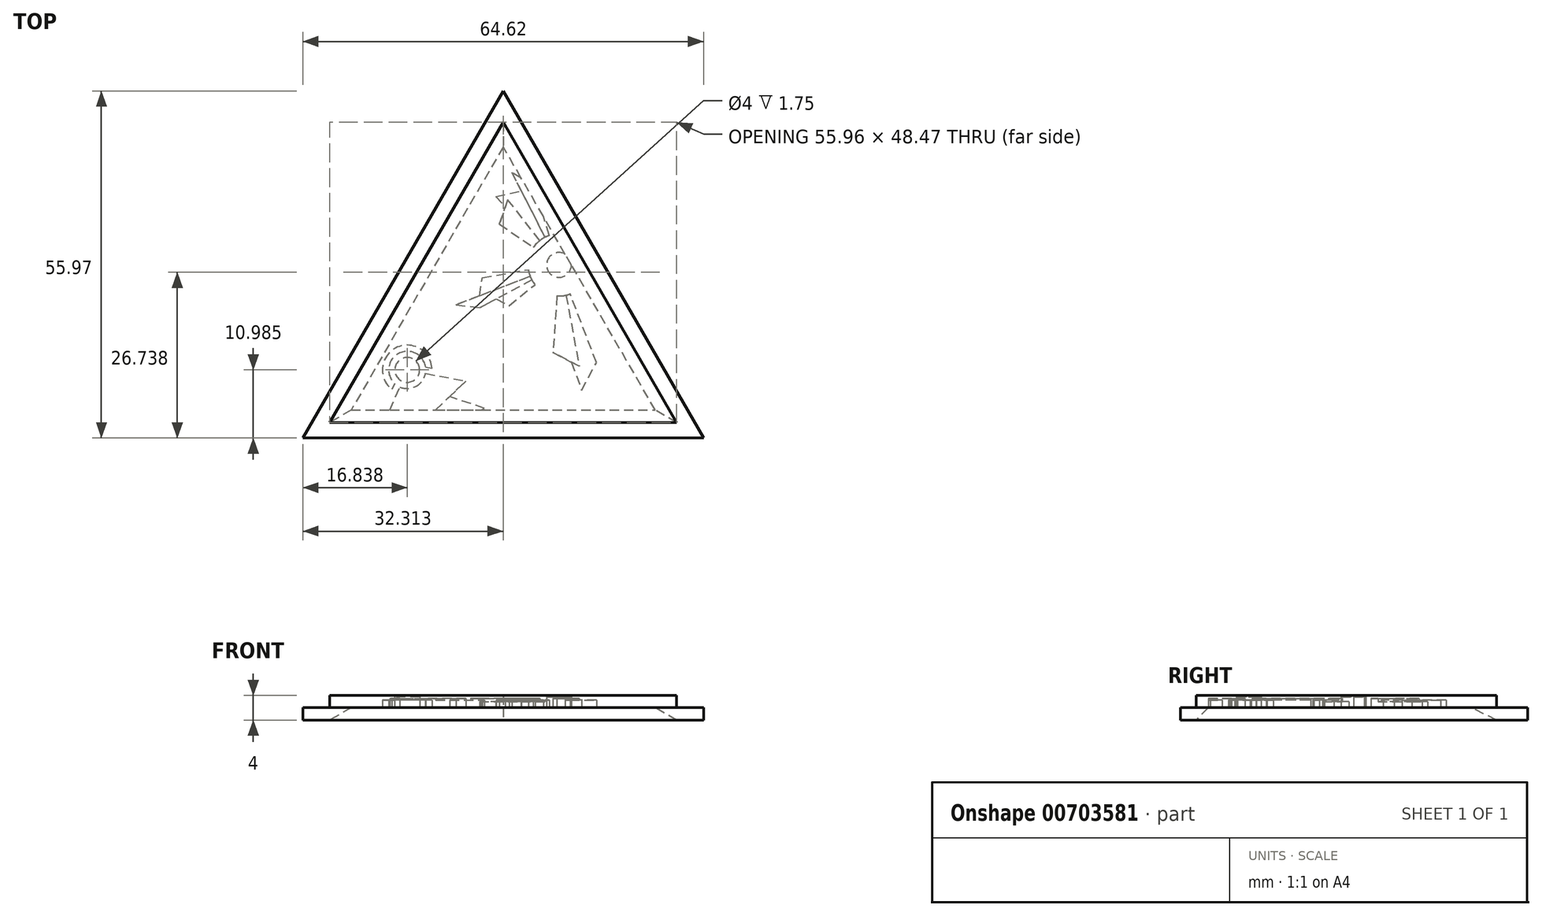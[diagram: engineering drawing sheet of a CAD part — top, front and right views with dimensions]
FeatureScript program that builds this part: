
annotation { "Feature Type Name" : "Feature", "Feature Type Description" : "" }
export const myFeature = defineFeature(function(context is Context, id is Id, definition is map)
    precondition{}
    {
        {
            var Q0;
            Q0=qCreatedBy(makeId("Top.planeOp"),FACE);
            var sketch = newSketch(context, id + "F0", { "sketchPlane" : qUnion([Q0])});
            skLineSegment(sketch, "E0", {"start": v(4.8, 63.3) * mm, "end": v(-23.18, 14.82) * mm});
            skLineSegment(sketch, "E1", {"start": v(-23.18, 14.82) * mm, "end": v(32.78, 14.82) * mm});
            skLineSegment(sketch, "E2", {"start": v(32.78, 14.82) * mm, "end": v(4.8, 63.3) * mm});
            skLineSegment(sketch, "E3", {"start": v(4.8, 68.3) * mm, "end": v(-27.5, 12.32) * mm});
            skLineSegment(sketch, "E4", {"start": v(-27.5, 12.32) * mm, "end": v(37.11, 12.32) * mm});
            skLineSegment(sketch, "E5", {"start": v(37.11, 12.32) * mm, "end": v(4.8, 68.3) * mm});
            skLineSegment(sketch, "E6", {"start": v(4.8, 59.3) * mm, "end": v(-19.72, 16.82) * mm});
            skLineSegment(sketch, "E7", {"start": v(-19.72, 16.82) * mm, "end": v(29.32, 16.82) * mm});
            skLineSegment(sketch, "E8", {"start": v(29.32, 16.82) * mm, "end": v(4.8, 59.3) * mm});
            skSolve(sketch);
        }
        {
            var Q0;
            Q0=makeQuery(id+"F0.imprint","IMPRINT",FACE,{"disambiguationData":[TD([[makeQuery(id+"F0.imprint","IMPRINT",EDGE,{"derivedFrom":sQuery(id+"F0.wireOp",EDGE,"E0")}),1.0]])]});
            extrude(context, id + "F1", {"entities" : qUnion([Q0]), "depth" : 4 * mm, "offsetDistance" : 25 * mm});
        }
        {
            var Q0;
            Q0=makeQuery(id+"F0.imprint","IMPRINT",FACE,{"disambiguationData":[TD([[makeQuery(id+"F0.imprint","IMPRINT",EDGE,{"derivedFrom":sQuery(id+"F0.wireOp",EDGE,"E0")}),-1.0]])]});
            extrude(context, id + "F2", {"entities" : qUnion([Q0]), "operationType" : NewBodyOperationType.ADD, "depth" : 2 * mm, "offsetDistance" : 25 * mm});
        }
        {
            var Q0;
            Q0=makeQuery(id+"F0.imprint","IMPRINT",FACE,{"disambiguationData":[TD([[makeQuery(id+"F0.imprint","IMPRINT",EDGE,{"derivedFrom":sQuery(id+"F0.wireOp",EDGE,"E6")}),1.0]])]});
            extrude(context, id + "F3", {"entities" : qUnion([Q0]), "operationType" : NewBodyOperationType.ADD, "depth" : 4 * mm, "offsetDistance" : 25 * mm, "hasSecondDirection" : true, "secondDirectionOppositeDirection" : true, "secondDirectionDepth" : -2 * mm});
        }
        {
            var Q0;
            Q0=makeQuery(id+"F1.opExtrude","CAP_EDGE",EDGE,{"disambiguationData":[OSD([sQuery(id+"F0.wireOp",EDGE,"E7")])],"isStart":true});
            var Q1;
            Q1=makeQuery(id+"F1.opExtrude","CAP_EDGE",EDGE,{"disambiguationData":[OSD([sQuery(id+"F0.wireOp",EDGE,"E6")])],"isStart":true});
            var Q2;
            Q2=makeQuery(id+"F1.opExtrude","CAP_EDGE",EDGE,{"disambiguationData":[OSD([sQuery(id+"F0.wireOp",EDGE,"E8")])],"isStart":true});
            chamfer(context, id + "F4", {"entities" : qUnion([Q0, Q1, Q2]), "width" : 2 * mm, "tangentPropagation" : true});
        }
        {
            var Q0;
            Q0=makeQuery(id+"F0.imprint","IMPRINT",FACE,{"disambiguationData":[TD([[makeQuery(id+"F0.imprint","IMPRINT",EDGE,{"derivedFrom":sQuery(id+"F0.wireOp",EDGE,"E6")}),1.0]])]});
            var sketch = newSketch(context, id + "F5", { "sketchPlane" : qUnion([Q0])});
            skCircle(sketch, "E9", {"center": v(13.8, 40.23) * mm, "radius": 4 * mm});
            skArc(sketch, "E10", {"start": v(13.46, 35.25) * mm, "mid": v(14.55, 35.29) * mm, "end": v(15.6, 35.57) * mm});
            skLineSegment(sketch, "E11", {"start": v(19.86, 24.49) * mm, "end": v(17.47, 20.03) * mm});
            skLineSegment(sketch, "E12", {"start": v(17.47, 20.03) * mm, "end": v(15.81, 24.55) * mm});
            skLineSegment(sketch, "E13", {"start": v(17.07, 23.88) * mm, "end": v(12.85, 26.14) * mm});
            skLineSegment(sketch, "E14", {"start": v(12.85, 26.14) * mm, "end": v(13.46, 35.25) * mm});
            skLineSegment(sketch, "E15.trimOffspring", {"start": v(14.94, 35.37) * mm, "end": v(17.07, 23.88) * mm});
            skLineSegment(sketch, "E16.trimOffspring", {"start": v(15.6, 35.57) * mm, "end": v(19.86, 24.49) * mm});
            skLineSegment(sketch, "E17", {"start": v(1.05, 33.34) * mm, "end": v(-2.82, 33.81) * mm});
            skLineSegment(sketch, "E18", {"start": v(-2.82, 33.81) * mm, "end": v(9.14, 38.43) * mm});
            skLineSegment(sketch, "E19", {"start": v(1.45, 38.2) * mm, "end": v(1, 35.28) * mm});
            skLineSegment(sketch, "E20.trimOffspring", {"start": v(9.42, 37.82) * mm, "end": v(1.05, 33.34) * mm});
            skLineSegment(sketch, "E21.trimOffspring", {"start": v(8.86, 39.48) * mm, "end": v(1.45, 38.2) * mm});
            skLineSegment(sketch, "E22", {"start": v(9.93, 37.06) * mm, "end": v(5.79, 33.66) * mm});
            skLineSegment(sketch, "E23", {"start": v(5.79, 33.66) * mm, "end": v(3.69, 34.76) * mm});
            skArc(sketch, "E24.trimOffspring", {"start": v(8.86, 39.48) * mm, "mid": v(9.23, 38.2) * mm, "end": v(9.93, 37.06) * mm});
            skCircle(sketch, "E25", {"center": v(13.8, 40.23) * mm, "radius": 2 * mm});
            skLineSegment(sketch, "E26", {"start": v(-18.6, 4.85) * mm, "end": v(-1.22, 21.5) * mm});
            skLineSegment(sketch, "E27", {"start": v(-1.22, 21.5) * mm, "end": v(-7.73, 22.74) * mm});
            skLineSegment(sketch, "E28", {"start": v(-11.86, 20.55) * mm, "end": v(-18.6, 4.85) * mm});
            skPoint(sketch, "E29.end.orphan", {"position": v(-18.6, 4.85) * mm});
            skLineSegment(sketch, "E30", {"start": v(-3.82, 19.01) * mm, "end": v(1.77, 17.12) * mm});
            skLineSegment(sketch, "E31", {"start": v(1.77, 17.12) * mm, "end": v(-18.6, 4.85) * mm});
            skArc(sketch, "E32", {"start": v(-7.7, 23.76) * mm, "mid": v(-12.08, 25.96) * mm, "end": v(-12.7, 21.1) * mm});
            skCircle(sketch, "E33", {"center": v(-10.67, 23.3) * mm, "radius": 2 * mm});
            skCircle(sketch, "E34", {"center": v(13.8, 40.23) * mm, "radius": 5 * mm});
            skLineSegment(sketch, "E35", {"start": v(5.54, 50.76) * mm, "end": v(4.21, 46.81) * mm});
            skLineSegment(sketch, "E36", {"start": v(9.68, 43.06) * mm, "end": v(4.21, 46.81) * mm});
            skLineSegment(sketch, "E37.trimOffspring", {"start": v(10.72, 44.17) * mm, "end": v(5.54, 50.76) * mm});
            skLineSegment(sketch, "E38", {"start": v(6.2, 55.17) * mm, "end": v(11.53, 44.69) * mm});
            skLineSegment(sketch, "E39", {"start": v(6.2, 55.17) * mm, "end": v(9.66, 53.08) * mm});
            skLineSegment(sketch, "E40", {"start": v(9.66, 53.08) * mm, "end": v(12.27, 45) * mm});
            skLineSegment(sketch, "E41", {"start": v(7.72, 52.17) * mm, "end": v(3.64, 51.29) * mm});
            skLineSegment(sketch, "E42.trimOffspring", {"start": v(5.16, 49.63) * mm, "end": v(3.64, 51.29) * mm});
            skArc(sketch, "E43", {"start": v(-6.68, 23.56) * mm, "mid": v(-12.55, 26.84) * mm, "end": v(-13.12, 20.14) * mm});
            skLineSegment(sketch, "E44", {"start": v(-6.68, 23.56) * mm, "end": v(-7.7, 23.76) * mm});
            skLineSegment(sketch, "E45", {"start": v(-13.12, 20.14) * mm, "end": v(-12.7, 21.1) * mm});
            skArc(sketch, "E46.trimOffspring", {"start": v(-11.86, 20.55) * mm, "mid": v(-9.27, 20.66) * mm, "end": v(-7.73, 22.74) * mm});
            skSolve(sketch);
        }
        {
            var Q0;
            {var subQ0=sQuery(id+"F5.wireOp",EDGE,"E25");var subQ1=makeQuery(id+"F0.imprint","IMPRINT",EDGE,{"derivedFrom":sQuery(id+"F0.wireOp",EDGE,"E8")});var subQ2=makeQuery(id+"F5.imprint","INTERSECT",VERTEX,{"disambiguationData":[OD(0.0)],"derivedFrom":[subQ1,subQ0]});Q0=makeQuery(id+"F5.imprint","IMPRINT",FACE,{"disambiguationData":[TD([[makeQuery(id+"F5.imprint","IMPRINT",EDGE,{"disambiguationData":[TD([[subQ2,-1.0]])],"derivedFrom":subQ0}),1.0]])]});}
            var Q1;
            Q1=makeQuery(id+"F5.imprint","IMPRINT",FACE,{"disambiguationData":[TD([[makeQuery(id+"F5.imprint","IMPRINT",EDGE,{"derivedFrom":sQuery(id+"F5.wireOp",EDGE,"E33")}),1.0]])]});
            extrude(context, id + "F6", {"entities" : qUnion([Q0, Q1]), "operationType" : NewBodyOperationType.REMOVE, "oppositeDirection" : true, "depth" : -3.75 * mm, "offsetDistance" : 25 * mm});
        }
        {
            var Q0;
            {var subQ7=sQuery(id+"F5.wireOp",EDGE,"E17");Q0=makeQuery(id+"F5.imprint","IMPRINT",FACE,{"disambiguationData":[TD([[makeQuery(id+"F5.imprint","IMPRINT",EDGE,{"derivedFrom":subQ7}),-1.0]])]});}
            var Q1;
            {var subQ0=sQuery(id+"F5.wireOp",EDGE,"E14");Q1=makeQuery(id+"F5.imprint","IMPRINT",FACE,{"disambiguationData":[TD([[makeQuery(id+"F5.imprint","IMPRINT",EDGE,{"derivedFrom":subQ0}),-1.0]])]});}
            var Q2;
            {var subQ5=sQuery(id+"F5.wireOp",EDGE,"E27");Q2=makeQuery(id+"F5.imprint","IMPRINT",FACE,{"disambiguationData":[TD([[makeQuery(id+"F5.imprint","IMPRINT",EDGE,{"derivedFrom":subQ5}),1.0]])]});}
            var Q3;
            {var subQ0=sQuery(id+"F5.wireOp",EDGE,"E36");Q3=makeQuery(id+"F5.imprint","IMPRINT",FACE,{"disambiguationData":[TD([[makeQuery(id+"F5.imprint","IMPRINT",EDGE,{"derivedFrom":subQ0}),-1.0]])]});}
            extrude(context, id + "F7", {"entities" : qUnion([Q0, Q1, Q2, Q3]), "operationType" : NewBodyOperationType.REMOVE, "oppositeDirection" : true, "depth" : -3.5 * mm, "offsetDistance" : 25 * mm});
        }
        {
            var Q0;
            Q0=makeQuery(id+"F5.imprint","IMPRINT",FACE,{"disambiguationData":[TD([[makeQuery(id+"F5.imprint","IMPRINT",EDGE,{"derivedFrom":sQuery(id+"F5.wireOp",EDGE,"E11")}),-1.0]])]});
            var Q1;
            {var subQ0=sQuery(id+"F5.wireOp",EDGE,"E30");Q1=makeQuery(id+"F5.imprint","IMPRINT",FACE,{"disambiguationData":[TD([[makeQuery(id+"F5.imprint","IMPRINT",EDGE,{"derivedFrom":subQ0}),-1.0]])]});}
            var Q2;
            {var subQ4=sQuery(id+"F5.wireOp",EDGE,"E22");Q2=makeQuery(id+"F5.imprint","IMPRINT",FACE,{"disambiguationData":[TD([[makeQuery(id+"F5.imprint","IMPRINT",EDGE,{"derivedFrom":subQ4}),-1.0]])]});}
            var Q3;
            {var subQ1=sQuery(id+"F5.wireOp",EDGE,"E38");var subQ5=sQuery(id+"F5.wireOp",EDGE,"E34");var subQ6=makeQuery(id+"F5.imprint","INTERSECT",VERTEX,{"derivedFrom":[subQ5,subQ1]});Q3=makeQuery(id+"F5.imprint","IMPRINT",FACE,{"disambiguationData":[TD([[makeQuery(id+"F5.imprint","IMPRINT",EDGE,{"disambiguationData":[TD([[subQ6,1.0]])],"derivedFrom":subQ5}),-1.0]])]});}
            var Q4;
            Q4=makeQuery(id+"F5.imprint","IMPRINT",FACE,{"disambiguationData":[TD([[makeQuery(id+"F5.imprint","IMPRINT",EDGE,{"derivedFrom":sQuery(id+"F5.wireOp",EDGE,"E32")}),-1.0]])]});
            extrude(context, id + "F8", {"entities" : qUnion([Q0, Q1, Q2, Q3, Q4]), "operationType" : NewBodyOperationType.REMOVE, "oppositeDirection" : true, "depth" : -3.25 * mm, "offsetDistance" : 25 * mm});
        }
        {
            var Q0;
            {var subQ3=sQuery(id+"F5.wireOp",EDGE,"E19");Q0=makeQuery(id+"F5.imprint","IMPRINT",FACE,{"disambiguationData":[TD([[makeQuery(id+"F5.imprint","IMPRINT",EDGE,{"derivedFrom":subQ3}),1.0]])]});}
            var Q1;
            {var subQ0=sQuery(id+"F5.wireOp",EDGE,"E37.trimOffspring");Q1=makeQuery(id+"F5.imprint","IMPRINT",FACE,{"disambiguationData":[TD([[makeQuery(id+"F5.imprint","IMPRINT",EDGE,{"derivedFrom":subQ0}),-1.0]])]});}
            extrude(context, id + "F9", {"entities" : qUnion([Q0, Q1]), "operationType" : NewBodyOperationType.REMOVE, "depth" : 3 * mm, "offsetDistance" : 25 * mm});
        }
    });
